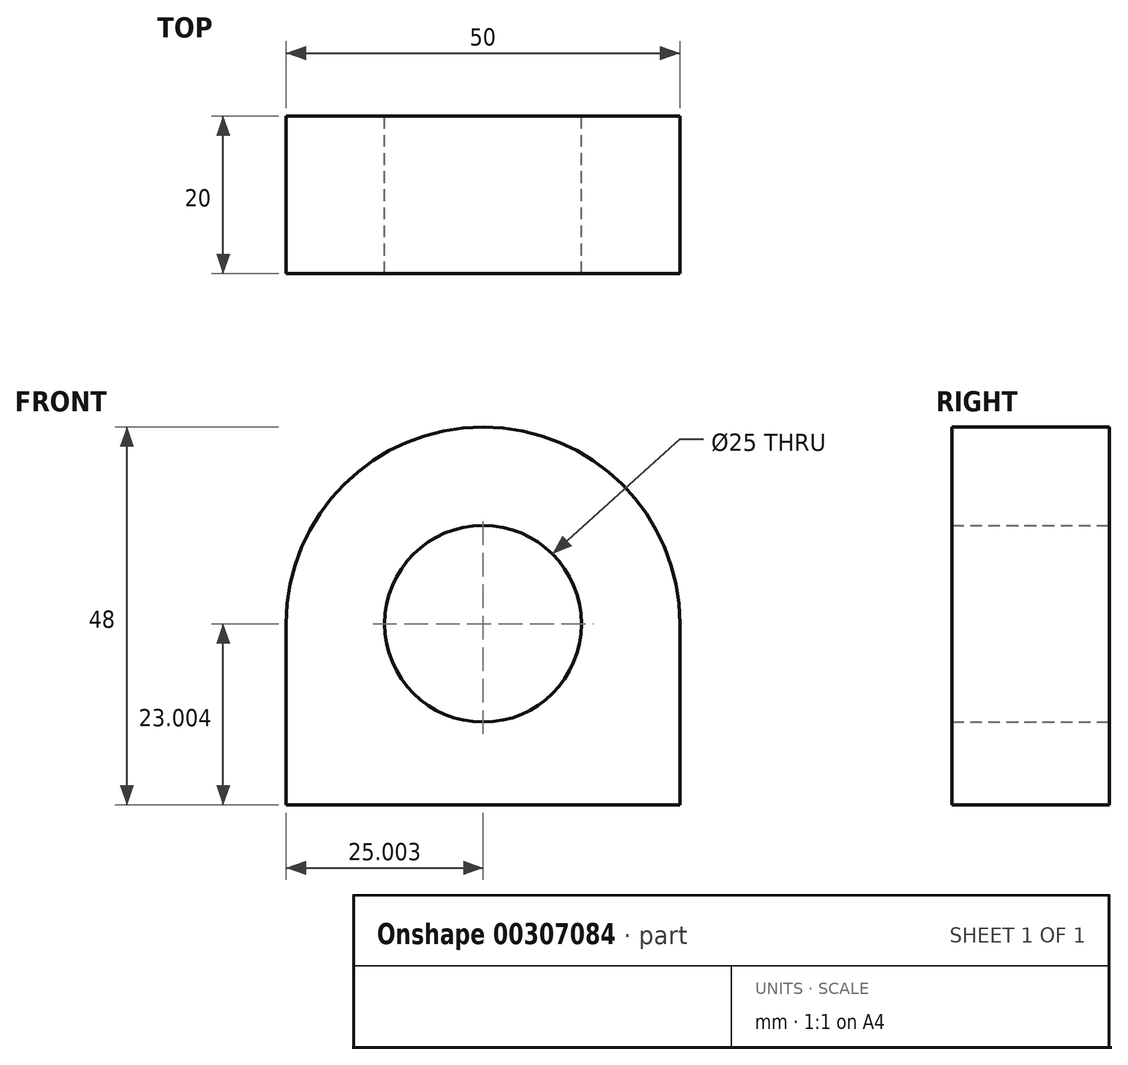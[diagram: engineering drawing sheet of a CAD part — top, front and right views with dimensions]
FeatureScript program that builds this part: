
annotation { "Feature Type Name" : "Feature", "Feature Type Description" : "" }
export const myFeature = defineFeature(function(context is Context, id is Id, definition is map)
    precondition{}
    {
        {
            var Q0;
            Q0=qCreatedBy(makeId("Front.planeOp"),FACE);
            var sketch = newSketch(context, id + "F0", { "sketchPlane" : qUnion([Q0])});
            skLineSegment(sketch, "E0.bottom", {"start": v(-45.6, 30.03) * mm, "end": v(4.4, 30.03) * mm});
            skLineSegment(sketch, "E0.top", {"start": v(-45.6, -17.97) * mm, "end": v(4.4, -17.97) * mm});
            skLineSegment(sketch, "E0.left", {"start": v(-45.6, 30.03) * mm, "end": v(-45.6, -17.97) * mm});
            skLineSegment(sketch, "E0.right", {"start": v(4.4, 30.03) * mm, "end": v(4.4, -17.97) * mm});
            skSolve(sketch);
        }
        {
            var Q0;
            Q0=makeQuery(id+"F0.imprint","IMPRINT",FACE,{"disambiguationData":[TD([[makeQuery(id+"F0.imprint","IMPRINT",EDGE,{"derivedFrom":sQuery(id+"F0.wireOp",EDGE,"E0.bottom")}),-1.0]])]});
            extrude(context, id + "F1", {"entities" : qUnion([Q0]), "depth" : 20 * mm});
        }
        {
            var Q0;
            Q0=makeQuery(id+"F1.opExtrude","SWEPT_EDGE",EDGE,{"disambiguationData":[OSD([sQuery(id+"F0.wireOp",EDGE,"E0.bottom"),sQuery(id+"F0.wireOp",EDGE,"E0.right")])]});
            var Q1;
            Q1=makeQuery(id+"F1.opExtrude","SWEPT_EDGE",EDGE,{"disambiguationData":[OSD([sQuery(id+"F0.wireOp",EDGE,"E0.bottom"),sQuery(id+"F0.wireOp",EDGE,"E0.left")])]});
            fillet(context, id + "F2", {"entities" : qUnion([Q0, Q1]), "radius" : 25 * mm, "tangentPropagation" : true, "allowEdgeOverflow" : false});
        }
        {
            var Q0;
            Q0=makeQuery(id+"F1.opExtrude","CAP_FACE",FACE,{"disambiguationData":[OSD([sQuery(id+"F0.wireOp",EDGE,"E0.bottom"),sQuery(id+"F0.wireOp",EDGE,"E0.top"),sQuery(id+"F0.wireOp",EDGE,"E0.left"),sQuery(id+"F0.wireOp",EDGE,"E0.right")])],"isStart":true});
            var sketch = newSketch(context, id + "F3", { "sketchPlane" : qUnion([Q0])});
            skCircle(sketch, "E1", {"center": v(20.6, 5.03) * mm, "radius": 12.5 * mm});
            skSolve(sketch);
        }
        {
            var Q0;
            Q0=makeQuery(id+"F3.imprint","IMPRINT",FACE,{"disambiguationData":[TD([[makeQuery(id+"F3.imprint","IMPRINT",EDGE,{"derivedFrom":sQuery(id+"F3.wireOp",EDGE,"E1")}),1.0]])]});
            extrude(context, id + "F4", {"entities" : qUnion([Q0]), "operationType" : NewBodyOperationType.REMOVE, "oppositeDirection" : true, "depth" : 25 * mm});
        }
    });
